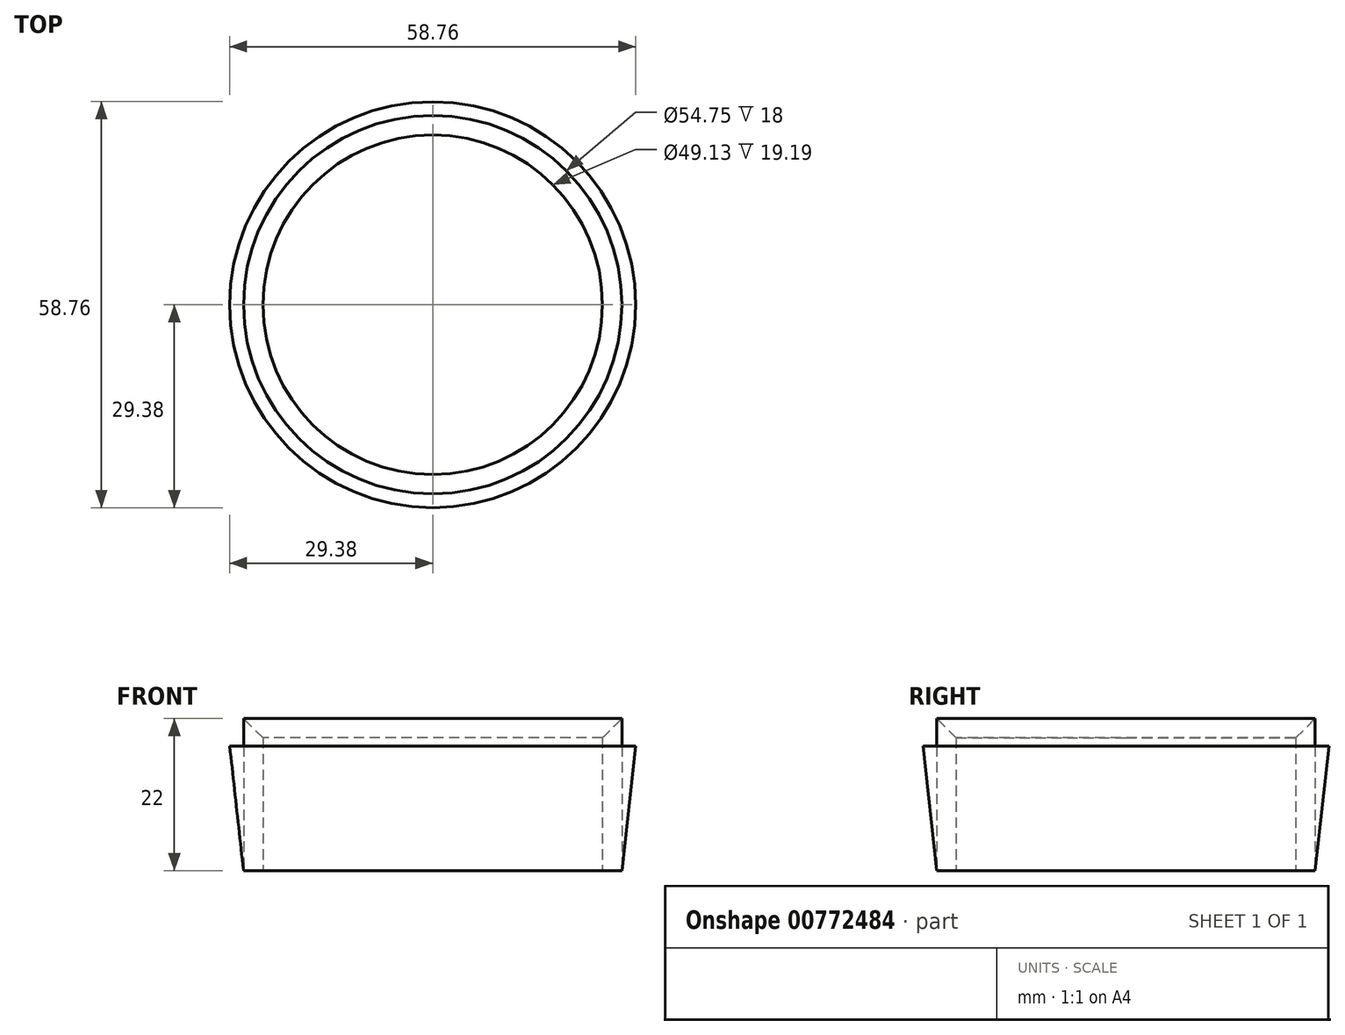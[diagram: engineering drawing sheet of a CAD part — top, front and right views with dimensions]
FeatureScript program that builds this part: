
annotation { "Feature Type Name" : "Feature", "Feature Type Description" : "" }
export const myFeature = defineFeature(function(context is Context, id is Id, definition is map)
    precondition{}
    {
        {
            var Q0;
            Q0=qCreatedBy(makeId("Top.planeOp"),FACE);
            var sketch = newSketch(context, id + "F0", { "sketchPlane" : qUnion([Q0])});
            skCircle(sketch, "E0", {"center": v(0, 0) * mm, "radius": 27.38 * mm});
            skCircle(sketch, "E1", {"center": v(0, 0) * mm, "radius": 24.57 * mm});
            skSolve(sketch);
        }
        {
            var Q0;
            Q0 = qSketchRegion(id + "F0", true);
            extrude(context, id + "F1", {"entities" : qUnion([Q0]), "depth" : 22.09 * mm, "offsetDistance" : 25 * mm});
        }
        {
            var Q0;
            Q0=makeQuery(id+"F1.opExtrude","CAP_EDGE",EDGE,{"disambiguationData":[OSD([sQuery(id+"F0.wireOp",EDGE,"E1")])],"isStart":false});
            chamfer(context, id + "F2", {"entities" : qUnion([Q0]), "chamferType" : ChamferType.OFFSET_ANGLE, "width" : 2.9 * mm, "oppositeDirection" : false, "angle" : 45 * degree, "tangentPropagation" : true});
        }
        {
            var Q0;
            Q0=qCreatedBy(makeId("Right.planeOp"),FACE);
            var sketch = newSketch(context, id + "F3", { "sketchPlane" : qUnion([Q0])});
            skLineSegment(sketch, "E2", {"start": v(-27.37, 0) * mm, "end": v(-29.38, 18) * mm});
            skLineSegment(sketch, "E3", {"start": v(-29.38, 18) * mm, "end": v(-27.38, 18) * mm});
            skLineSegment(sketch, "E4", {"start": v(-27.38, 18) * mm, "end": v(-27.38, 0) * mm});
            skSolve(sketch);
        }
        {
            var Q0;
            Q0=qCreatedBy(makeId("Right.planeOp"),FACE);
            var sketch = newSketch(context, id + "F4", { "sketchPlane" : qUnion([Q0])});
            skLineSegment(sketch, "E5", {"start": v(0, 0) * mm, "end": v(0, 15.7) * mm, "construction": true});
            skSolve(sketch);
        }
        {
            var Q0;
            Q0=makeQuery(id+"F3.imprint","IMPRINT",FACE,{"disambiguationData":[TD([[makeQuery(id+"F3.imprint","IMPRINT",EDGE,{"derivedFrom":sQuery(id+"F3.wireOp",EDGE,"E2")}),-1.0]])]});
            var Q1;
            Q1=sQuery(id+"F4.wireOp",EDGE,"E5");
            revolve(context, id + "F5", {"surfaceOperationType" : NewSurfaceOperationType.NEW, "entities" : qUnion([Q0]), "axis" : qUnion([Q1]), "revolveType" : RevolveType.FULL});
        }
    });
